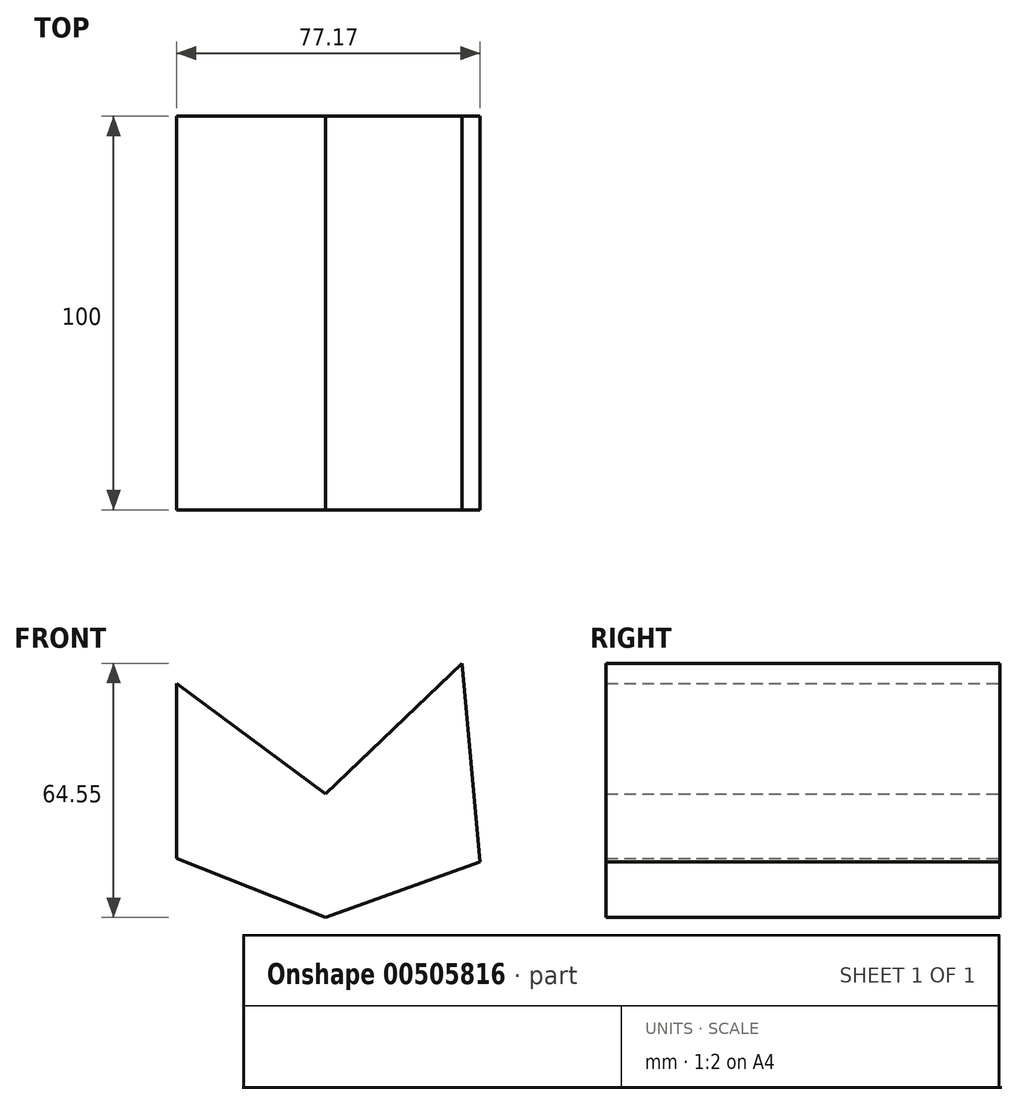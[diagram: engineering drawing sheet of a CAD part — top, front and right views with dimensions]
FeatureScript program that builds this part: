
annotation { "Feature Type Name" : "Feature", "Feature Type Description" : "" }
export const myFeature = defineFeature(function(context is Context, id is Id, definition is map)
    precondition{}
    {
        {
            var Q0;
            Q0=qCreatedBy(makeId("Front.planeOp"),FACE);
            var sketch = newSketch(context, id + "F0", { "sketchPlane" : qUnion([Q0])});
            skLineSegment(sketch, "E0", {"start": v(0, 0) * mm, "end": v(-37.87, 27.97) * mm});
            skLineSegment(sketch, "E1", {"start": v(0, 0) * mm, "end": v(34.71, 33.14) * mm});
            skLineSegment(sketch, "E2", {"start": v(34.71, 33.14) * mm, "end": v(39.3, -17.36) * mm});
            skLineSegment(sketch, "E3", {"start": v(-37.87, 27.97) * mm, "end": v(-37.87, -16.5) * mm});
            skLineSegment(sketch, "E4", {"start": v(-37.87, -16.5) * mm, "end": v(0, -31.41) * mm});
            skLineSegment(sketch, "E5", {"start": v(39.3, -17.36) * mm, "end": v(0, -31.41) * mm});
            skSolve(sketch);
        }
        {
            var Q0;
            Q0 = qSketchRegion(id + "F0", true);
            extrude(context, id + "F1", {"entities" : qUnion([Q0]), "depth" : 100 * mm});
        }
    });
